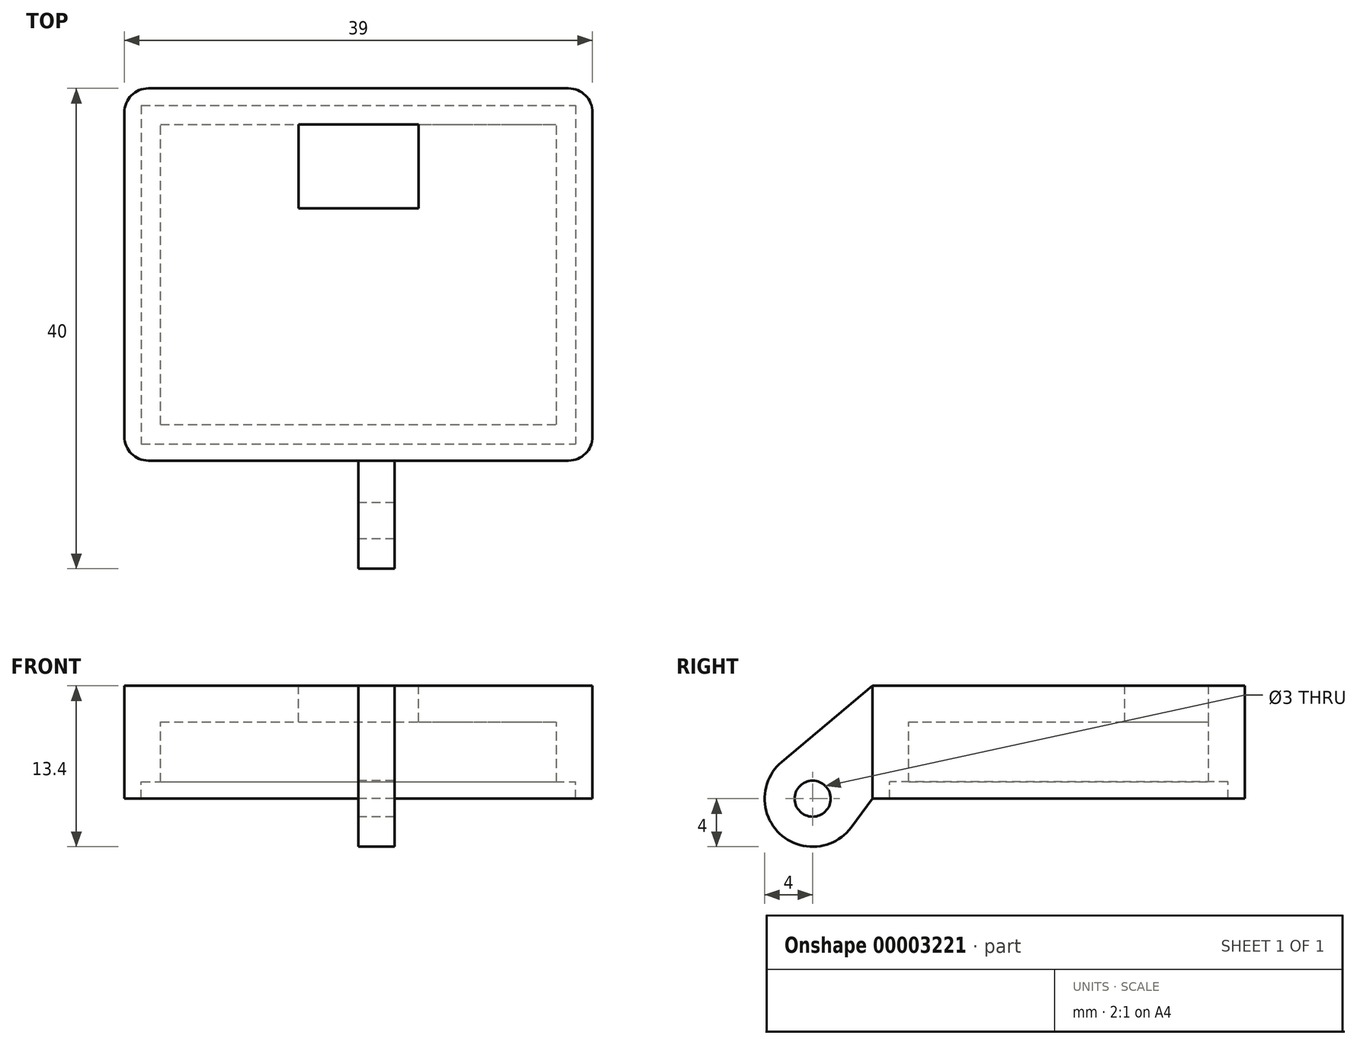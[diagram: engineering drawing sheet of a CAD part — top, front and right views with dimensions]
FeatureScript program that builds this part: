
annotation { "Feature Type Name" : "Feature", "Feature Type Description" : "" }
export const myFeature = defineFeature(function(context is Context, id is Id, definition is map)
    precondition{}
    {
        {
            var Q0;
            Q0=qCreatedBy(makeId("Top.planeOp"),FACE);
            var sketch = newSketch(context, id + "F0", { "sketchPlane" : qUnion([Q0])});
            skLineSegment(sketch, "E0.rect.bottom", {"start": v(-17.5, -15.5) * mm, "end": v(17.5, -15.5) * mm});
            skLineSegment(sketch, "E0.rect.top", {"start": v(-17.5, 15.5) * mm, "end": v(17.5, 15.5) * mm});
            skLineSegment(sketch, "E0.rect.left", {"start": v(-19.5, -13.5) * mm, "end": v(-19.5, 13.5) * mm});
            skLineSegment(sketch, "E0.rect.right", {"start": v(19.5, -13.5) * mm, "end": v(19.5, 13.5) * mm});
            skPoint(sketch, "E0.rect.middle", {"position": v(0, 0) * mm});
            skPoint(sketch, "E1.visualSharp", {"position": v(-19.5, 15.5) * mm});
            skArc(sketch, "E1.filletArc", {"start": v(-17.5, 15.5) * mm, "mid": v(-18.91, 14.91) * mm, "end": v(-19.5, 13.5) * mm});
            skPoint(sketch, "E2.visualSharp", {"position": v(-19.5, -15.5) * mm});
            skArc(sketch, "E2.filletArc", {"start": v(-19.5, -13.5) * mm, "mid": v(-18.91, -14.91) * mm, "end": v(-17.5, -15.5) * mm});
            skPoint(sketch, "E3.visualSharp", {"position": v(19.5, -15.5) * mm});
            skArc(sketch, "E3.filletArc", {"start": v(17.5, -15.5) * mm, "mid": v(18.91, -14.91) * mm, "end": v(19.5, -13.5) * mm});
            skPoint(sketch, "E4.visualSharp", {"position": v(19.5, 15.5) * mm});
            skArc(sketch, "E4.filletArc", {"start": v(19.5, 13.5) * mm, "mid": v(18.91, 14.91) * mm, "end": v(17.5, 15.5) * mm});
            skSolve(sketch);
        }
        {
            var Q0;
            Q0=makeQuery(id+"F0.imprint","IMPRINT",FACE,{"disambiguationData":[TD([[makeQuery(id+"F0.imprint","IMPRINT",EDGE,{"derivedFrom":sQuery(id+"F0.wireOp",EDGE,"E0.rect.bottom")}),1.0]])]});
            extrude(context, id + "F1", {"entities" : qUnion([Q0]), "oppositeDirection" : true, "depth" : 9.4 * mm});
        }
        {
            var Q0;
            Q0=makeQuery(id+"F1.opExtrude","CAP_FACE",FACE,{"disambiguationData":[OSD([sQuery(id+"F0.wireOp",EDGE,"E0.rect.bottom"),sQuery(id+"F0.wireOp",EDGE,"E0.rect.top"),sQuery(id+"F0.wireOp",EDGE,"E0.rect.left"),sQuery(id+"F0.wireOp",EDGE,"E0.rect.right"),sQuery(id+"F0.wireOp",EDGE,"E1.filletArc"),sQuery(id+"F0.wireOp",EDGE,"E2.filletArc"),sQuery(id+"F0.wireOp",EDGE,"E3.filletArc"),sQuery(id+"F0.wireOp",EDGE,"E4.filletArc")])],"isStart":false});
            shell(context, id + "F2", {"entities" : qUnion([Q0]), "thickness" : 3 * mm});
        }
        {
            var Q0;
            Q0=qCreatedBy(makeId("Front.planeOp"),FACE);
            var sketch = newSketch(context, id + "F3", { "sketchPlane" : qUnion([Q0])});
            skLineSegment(sketch, "E5.rect.bottom", {"start": v(-18.1, -9.4) * mm, "end": v(18.1, -9.4) * mm});
            skLineSegment(sketch, "E5.rect.top", {"start": v(-18.1, -8) * mm, "end": v(18.1, -8) * mm});
            skLineSegment(sketch, "E5.rect.left", {"start": v(-18.1, -9.4) * mm, "end": v(-18.1, -8) * mm});
            skLineSegment(sketch, "E5.rect.right", {"start": v(18.1, -9.4) * mm, "end": v(18.1, -8) * mm});
            skPoint(sketch, "E5.rect.middle", {"position": v(0, -8.7) * mm});
            skLineSegment(sketch, "E6", {"start": v(0, 0) * mm, "end": v(0, -8) * mm, "construction": true});
            skSolve(sketch);
        }
        {
            var Q0;
            Q0=makeQuery(id+"F3.imprint","IMPRINT",FACE,{"disambiguationData":[TD([[makeQuery(id+"F3.imprint","IMPRINT",EDGE,{"derivedFrom":sQuery(id+"F3.wireOp",EDGE,"E5.rect.bottom")}),1.0]])]});
            extrude(context, id + "F4", {"entities" : qUnion([Q0]), "operationType" : NewBodyOperationType.REMOVE, "endBound" : BoundingType.SYMMETRIC, "oppositeDirection" : true, "depth" : 28.2 * mm});
        }
        {
            var Q0;
            Q0=qCreatedBy(makeId("Right.planeOp"),FACE);
            var sketch = newSketch(context, id + "F5", { "sketchPlane" : qUnion([Q0])});
            skLineSegment(sketch, "E7", {"start": v(0, 0) * mm, "end": v(-15.5, 0) * mm, "construction": true});
            skLineSegment(sketch, "E8", {"start": v(-15.5, 0) * mm, "end": v(-15.5, -9.4) * mm});
            skArc(sketch, "E9", {"start": v(-23.07, -6.33) * mm, "mid": v(-23.25, -12.3) * mm, "end": v(-17.3, -11.8) * mm});
            skLineSegment(sketch, "E10", {"start": v(-15.5, 0) * mm, "end": v(-23.07, -6.33) * mm});
            skLineSegment(sketch, "E11", {"start": v(-15.5, -9.4) * mm, "end": v(-17.3, -11.8) * mm});
            skLineSegment(sketch, "E12", {"start": v(-15.5, -9.4) * mm, "end": v(-15.5, -13.4) * mm, "construction": true});
            skLineSegment(sketch, "E13", {"start": v(-15.5, -13.4) * mm, "end": v(-20.01, -13.4) * mm, "construction": true});
            skLineSegment(sketch, "E14", {"start": v(-15.5, -9.4) * mm, "end": v(-20.5, -9.4) * mm, "construction": true});
            skSolve(sketch);
        }
        {
            var Q0;
            Q0=makeQuery(id+"F5.imprint","IMPRINT",FACE,{"disambiguationData":[TD([[makeQuery(id+"F5.imprint","IMPRINT",EDGE,{"derivedFrom":sQuery(id+"F5.wireOp",EDGE,"E8")}),-1.0]])]});
            extrude(context, id + "F6", {"entities" : qUnion([Q0]), "operationType" : NewBodyOperationType.ADD, "depth" : 3 * mm});
        }
        {
            var Q0;
            Q0=makeQuery(id+"F6.opExtrude","CAP_FACE",FACE,{"disambiguationData":[OSD([sQuery(id+"F5.wireOp",EDGE,"E8"),sQuery(id+"F5.wireOp",EDGE,"E9"),sQuery(id+"F5.wireOp",EDGE,"E10"),sQuery(id+"F5.wireOp",EDGE,"E11")])],"isStart":true});
            var sketch = newSketch(context, id + "F7", { "sketchPlane" : qUnion([Q0])});
            skCircle(sketch, "E15", {"center": v(20.5, -9.4) * mm, "radius": 1.5 * mm});
            skSolve(sketch);
        }
        {
            var Q0;
            Q0=makeQuery(id+"F7.imprint","IMPRINT",FACE,{"disambiguationData":[TD([[makeQuery(id+"F7.imprint","IMPRINT",EDGE,{"derivedFrom":sQuery(id+"F7.wireOp",EDGE,"E15")}),1.0]])]});
            extrude(context, id + "F8", {"entities" : qUnion([Q0]), "operationType" : NewBodyOperationType.REMOVE, "endBound" : BoundingType.THROUGH_ALL, "oppositeDirection" : true, "depth" : 25 * mm});
        }
        {
            var Q0;
            Q0=makeQuery(id+"F1.opExtrude","CAP_FACE",FACE,{"disambiguationData":[OSD([sQuery(id+"F0.wireOp",EDGE,"E0.rect.bottom"),sQuery(id+"F0.wireOp",EDGE,"E0.rect.top"),sQuery(id+"F0.wireOp",EDGE,"E0.rect.left"),sQuery(id+"F0.wireOp",EDGE,"E0.rect.right"),sQuery(id+"F0.wireOp",EDGE,"E1.filletArc"),sQuery(id+"F0.wireOp",EDGE,"E2.filletArc"),sQuery(id+"F0.wireOp",EDGE,"E3.filletArc"),sQuery(id+"F0.wireOp",EDGE,"E4.filletArc")])],"isStart":true});
            var sketch = newSketch(context, id + "F9", { "sketchPlane" : qUnion([Q0])});
            skLineSegment(sketch, "E16.rect.bottom", {"start": v(-5, 5.5) * mm, "end": v(5, 5.5) * mm});
            skLineSegment(sketch, "E16.rect.top", {"start": v(-5, 12.5) * mm, "end": v(5, 12.5) * mm});
            skLineSegment(sketch, "E16.rect.left", {"start": v(-5, 5.5) * mm, "end": v(-5, 12.5) * mm});
            skLineSegment(sketch, "E16.rect.right", {"start": v(5, 5.5) * mm, "end": v(5, 12.5) * mm});
            skPoint(sketch, "E16.rect.middle", {"position": v(0, 9) * mm});
            skLineSegment(sketch, "E17", {"start": v(0, 0) * mm, "end": v(0, 12.5) * mm, "construction": true});
            skSolve(sketch);
        }
        {
            var Q0;
            Q0=makeQuery(id+"F9.imprint","IMPRINT",FACE,{"disambiguationData":[TD([[makeQuery(id+"F9.imprint","IMPRINT",EDGE,{"derivedFrom":sQuery(id+"F9.wireOp",EDGE,"E16.rect.bottom")}),1.0]])]});
            extrude(context, id + "F10", {"entities" : qUnion([Q0]), "operationType" : NewBodyOperationType.REMOVE, "endBound" : BoundingType.THROUGH_ALL, "oppositeDirection" : true, "depth" : 25 * mm});
        }
    });
